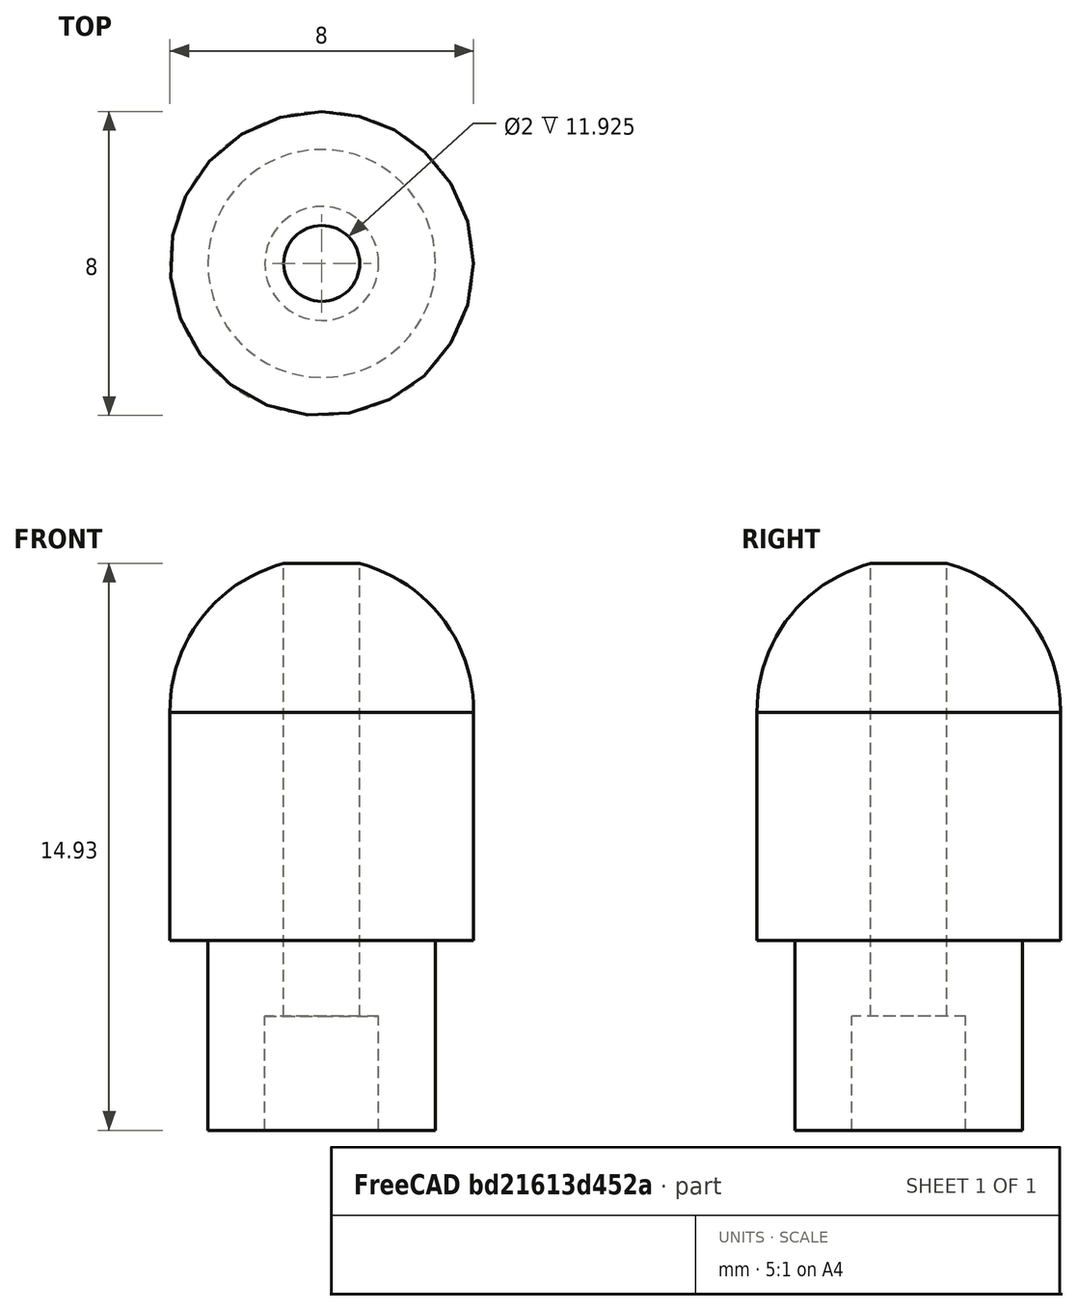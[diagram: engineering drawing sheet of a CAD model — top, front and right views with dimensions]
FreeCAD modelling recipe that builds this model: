
FCSTD DOCUMENT  (FreeCAD 0.16R6712 (Git))
Label: Head
License: All rights reserved
LicenseURL: http://en.wikipedia.org/wiki/All_rights_reserved
objects: Sketcher::SketchObject×1, PartDesign::Revolution×1
note: 3 computed .brp shape members not serialized (recipe doc carries the construction recipe); baked Part::Feature solids carry a one-line shape summary decoded from their .brp

FEATURE [Sketcher::SketchObject] Sketch
  Placement = pos=(0,0,300) rot=(0,1,0;1.5708rad)
  sketch-geometry (8):
    g0: LineSegment StartX=1e-12 StartY=4 StartZ=0 EndX=6 EndY=4 EndZ=0
    g1: LineSegment StartX=6 StartY=4 StartZ=0 EndX=6 EndY=3 EndZ=0
    g2: LineSegment StartX=6 StartY=3 StartZ=0 EndX=11 EndY=3 EndZ=0
    g3: LineSegment StartX=11 StartY=3 StartZ=0 EndX=11 EndY=1.5 EndZ=0
    g4: LineSegment StartX=11 StartY=1.5 StartZ=0 EndX=8 EndY=1.5 EndZ=0
    g5: LineSegment StartX=8 StartY=1.5 StartZ=0 EndX=8 EndY=1 EndZ=0
    g6: ArcOfCircle CenterX=-0.0520403 CenterY=0.000338538 CenterZ=0 NormalX=0 NormalY=0 NormalZ=1 Radius=4 StartAngle=1.55779 EndAngle=2.889
    g7: LineSegment StartX=8 StartY=1 StartZ=0 EndX=-3.92511 EndY=1 EndZ=0
  constraints (22):
    c: Horizontal(g0)
    c: DistanceY(g-1,g0) = 4
    c: Coincident(g1,g0)
    c: Vertical(g1)
    c: Coincident(g2,g1)
    c: Horizontal(g2)
    c: Coincident(g3,g2)
    c: Vertical(g3)
    c: Coincident(g4,g3)
    c: Horizontal(g4)
    c: Coincident(g5,g4)
    c: Vertical(g5)
    c: DistanceY(g-1,g1) = 3
    c: DistanceX(g2,g2) = 5
    c: DistanceX(g4,g4) = 3
    c: DistanceY(g-1,g5) = 1
    c: DistanceY(g-1,g3) = 1.5
    c: Coincident(g6,g0)
    c: Radius(g6) = 4
    c: Coincident(g7,g5)
    c: Coincident(g7,g6)
    c: Horizontal(g7)
FEATURE [PartDesign::Revolution] Revolution
  Angle = 360
  Axis = (0,0,-1)
  Base = (0,0,300)
  Placement = pos=(0,0,300) rot=(0,1,0;1.5708rad)
  ReferenceAxis = -> Sketch [H_Axis]
  Sketch = -> Sketch
